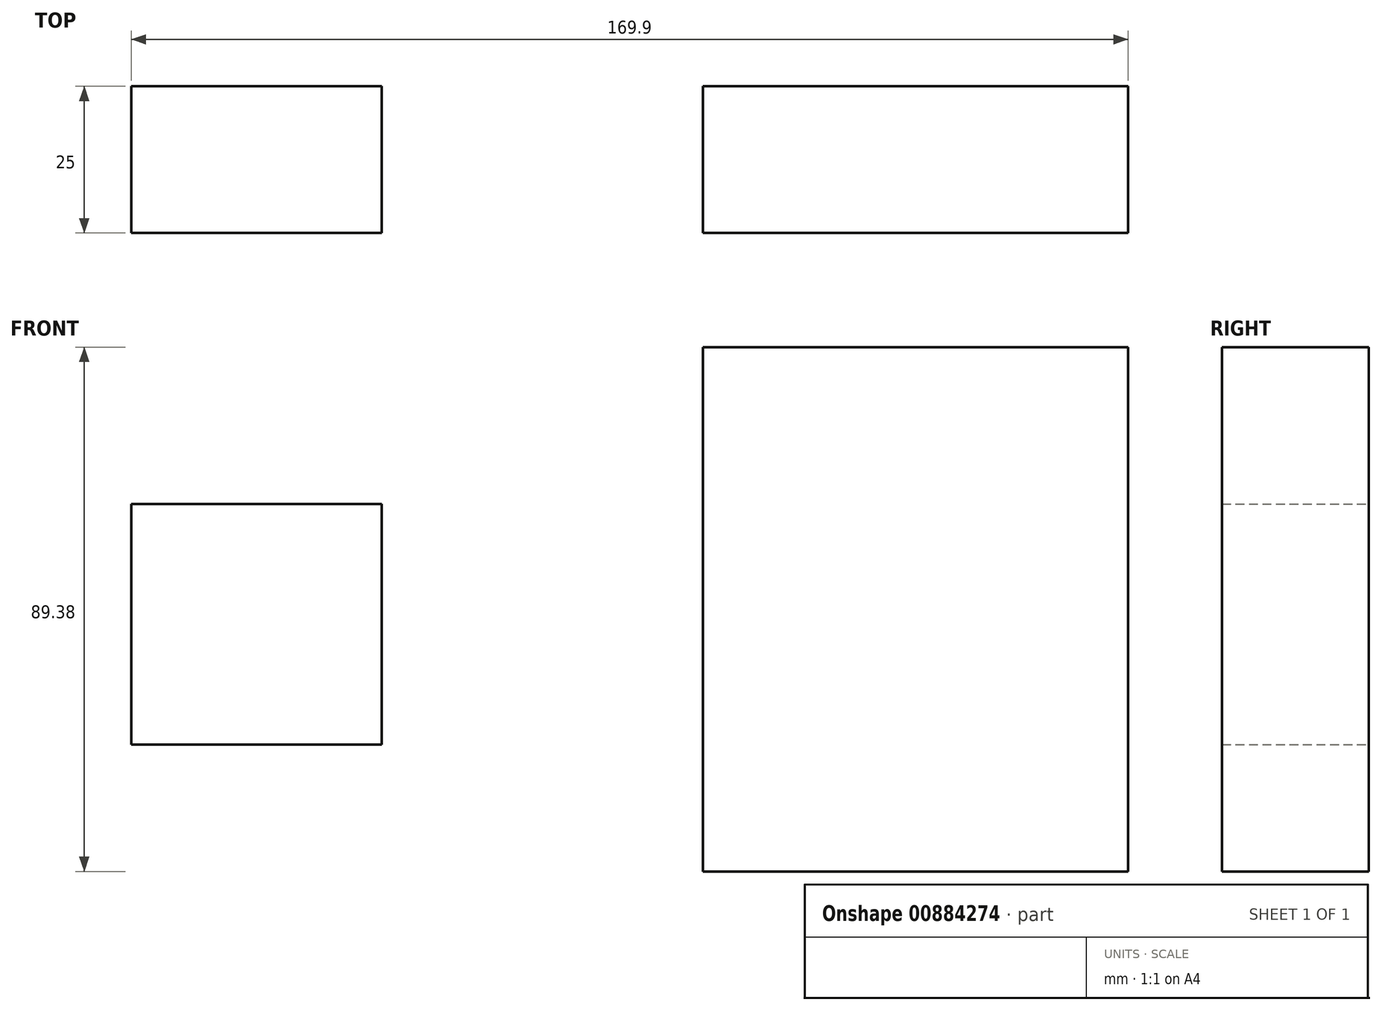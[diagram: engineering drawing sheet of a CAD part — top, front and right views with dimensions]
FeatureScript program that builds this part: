
annotation { "Feature Type Name" : "Feature", "Feature Type Description" : "" }
export const myFeature = defineFeature(function(context is Context, id is Id, definition is map)
    precondition{}
    {
        {
            var Q0;
            Q0=qCreatedBy(makeId("Front.planeOp"),FACE);
            var sketch = newSketch(context, id + "F0", { "sketchPlane" : qUnion([Q0])});
            skLineSegment(sketch, "E0.bottom", {"start": v(-133.68, 3.3) * mm, "end": v(-90.96, 3.3) * mm});
            skLineSegment(sketch, "E0.top", {"start": v(-133.68, 44.34) * mm, "end": v(-90.96, 44.34) * mm});
            skLineSegment(sketch, "E0.left", {"start": v(-133.68, 3.3) * mm, "end": v(-133.68, 44.34) * mm});
            skLineSegment(sketch, "E0.right", {"start": v(-90.96, 3.3) * mm, "end": v(-90.96, 44.34) * mm});
            skPoint(sketch, "E0.middle", {"position": v(-112.32, 23.82) * mm});
            skLineSegment(sketch, "E1.bottom", {"start": v(-36.22, -18.3) * mm, "end": v(36.22, -18.3) * mm});
            skLineSegment(sketch, "E1.top", {"start": v(-36.22, 71.08) * mm, "end": v(36.22, 71.08) * mm});
            skLineSegment(sketch, "E1.left", {"start": v(-36.22, -18.3) * mm, "end": v(-36.22, 71.08) * mm});
            skLineSegment(sketch, "E1.right", {"start": v(36.22, -18.3) * mm, "end": v(36.22, 71.08) * mm});
            skPoint(sketch, "E1.middle", {"position": v(0, 26.4) * mm});
            skSolve(sketch);
        }
        {
            var Q0;
            Q0 = qSketchRegion(id + "F0", true);
            extrude(context, id + "F1", {"entities" : qUnion([Q0]), "depth" : 25 * mm, "offsetDistance" : 25 * mm});
        }
    });
